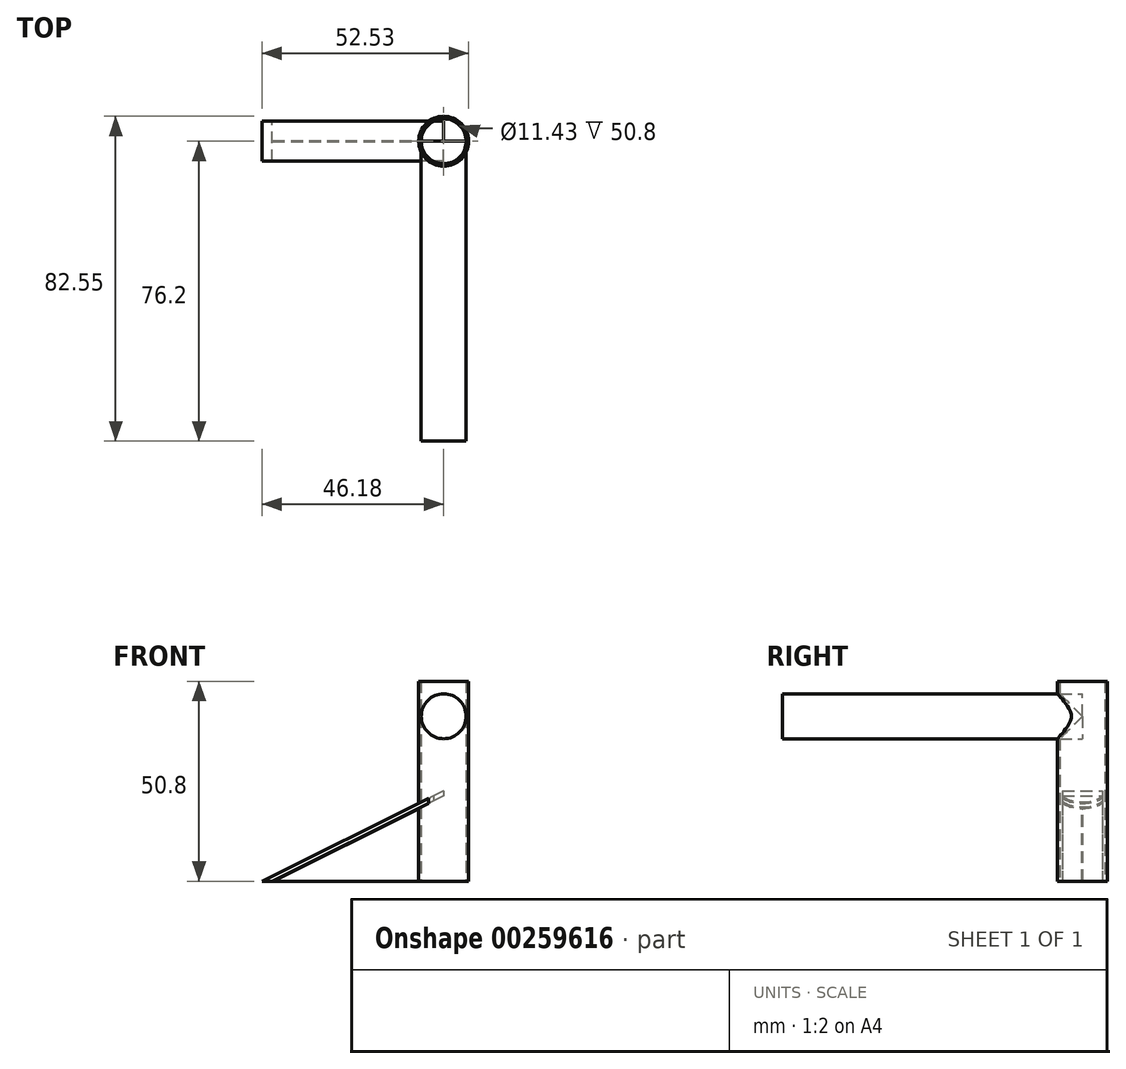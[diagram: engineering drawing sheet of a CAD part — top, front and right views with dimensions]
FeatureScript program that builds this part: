
annotation { "Feature Type Name" : "Feature", "Feature Type Description" : "" }
export const myFeature = defineFeature(function(context is Context, id is Id, definition is map)
    precondition{}
    {
        {
            var Q0;
            Q0=qCreatedBy(makeId("Top.planeOp"),FACE);
            var sketch = newSketch(context, id + "F0", { "sketchPlane" : qUnion([Q0])});
            skCircle(sketch, "E0", {"center": v(0, 0) * mm, "radius": 5.72 * mm});
            skCircle(sketch, "E1", {"center": v(0, 0) * mm, "radius": 6.35 * mm});
            skSolve(sketch);
        }
        {
            var Q0;
            Q0=makeQuery(id+"F0.imprint","IMPRINT",FACE,{"disambiguationData":[TD([[makeQuery(id+"F0.imprint","IMPRINT",EDGE,{"derivedFrom":sQuery(id+"F0.wireOp",EDGE,"E0")}),-1.0]])]});
            extrude(context, id + "F1", {"entities" : qUnion([Q0]), "depth" : 50.8 * mm});
        }
        {
            var Q0;
            Q0=qCreatedBy(makeId("Front.planeOp"),FACE);
            var sketch = newSketch(context, id + "F2", { "sketchPlane" : qUnion([Q0])});
            skCircle(sketch, "E2", {"center": v(0, 41.91) * mm, "radius": 5.72 * mm});
            skSolve(sketch);
        }
        {
            var Q0;
            Q0=qSketchRegion(id+"F2",true);
            extrude(context, id + "F3", {"entities" : qUnion([Q0]), "operationType" : NewBodyOperationType.ADD, "depth" : 76.2 * mm});
        }
        {
            var Q0;
            Q0=qCreatedBy(makeId("Front.planeOp"),FACE);
            var sketch = newSketch(context, id + "F4", { "sketchPlane" : qUnion([Q0])});
            skLineSegment(sketch, "E3", {"start": v(0, 22.94) * mm, "end": v(0, 21.67) * mm});
            skLineSegment(sketch, "E4", {"start": v(43.63, 0) * mm, "end": v(46.18, 0) * mm});
            skLineSegment(sketch, "E5.MirrorCS", {"start": v(-43.63, 0) * mm, "end": v(-46.18, 0) * mm});
            skLineSegment(sketch, "E6.MirrorCS", {"start": v(0, 22.94) * mm, "end": v(-46.18, 0) * mm});
            skLineSegment(sketch, "E7.MirrorCS", {"start": v(0, 21.67) * mm, "end": v(-43.63, 0) * mm});
            skSolve(sketch);
        }
        {
            var Q0;
            Q0=makeQuery(id+"F4.imprint","IMPRINT",FACE,{"disambiguationData":[TD([[makeQuery(id+"F4.imprint","IMPRINT",EDGE,{"derivedFrom":sQuery(id+"F4.wireOp",EDGE,"E5.MirrorCS")}),-1.0]])]});
            extrude(context, id + "F5", {"entities" : qUnion([Q0]), "operationType" : NewBodyOperationType.ADD, "depth" : 10.16 * mm, "symmetric" : true});
        }
        {
            var Q0;
            Q0=qCreatedBy(makeId("Front.planeOp"),FACE);
            var sketch = newSketch(context, id + "F6", { "sketchPlane" : qUnion([Q0])});
            skLineSegment(sketch, "E8.MirrorCS", {"start": v(-43.38, 0) * mm, "end": v(-6.45, 18.36) * mm});
            skLineSegment(sketch, "E9.MirrorCS", {"start": v(-6.45, 18.36) * mm, "end": v(-6.45, 0) * mm});
            skLineSegment(sketch, "E10.MirrorCS", {"start": v(-6.45, 0) * mm, "end": v(-43.38, 0) * mm});
            skSolve(sketch);
        }
        {
            var Q0;
            Q0=qSketchRegion(id+"F6",true);
            extrude(context, id + "F7", {"entities" : qUnion([Q0]), "depth" : 0.25 * mm, "symmetric" : true});
        }
    });
